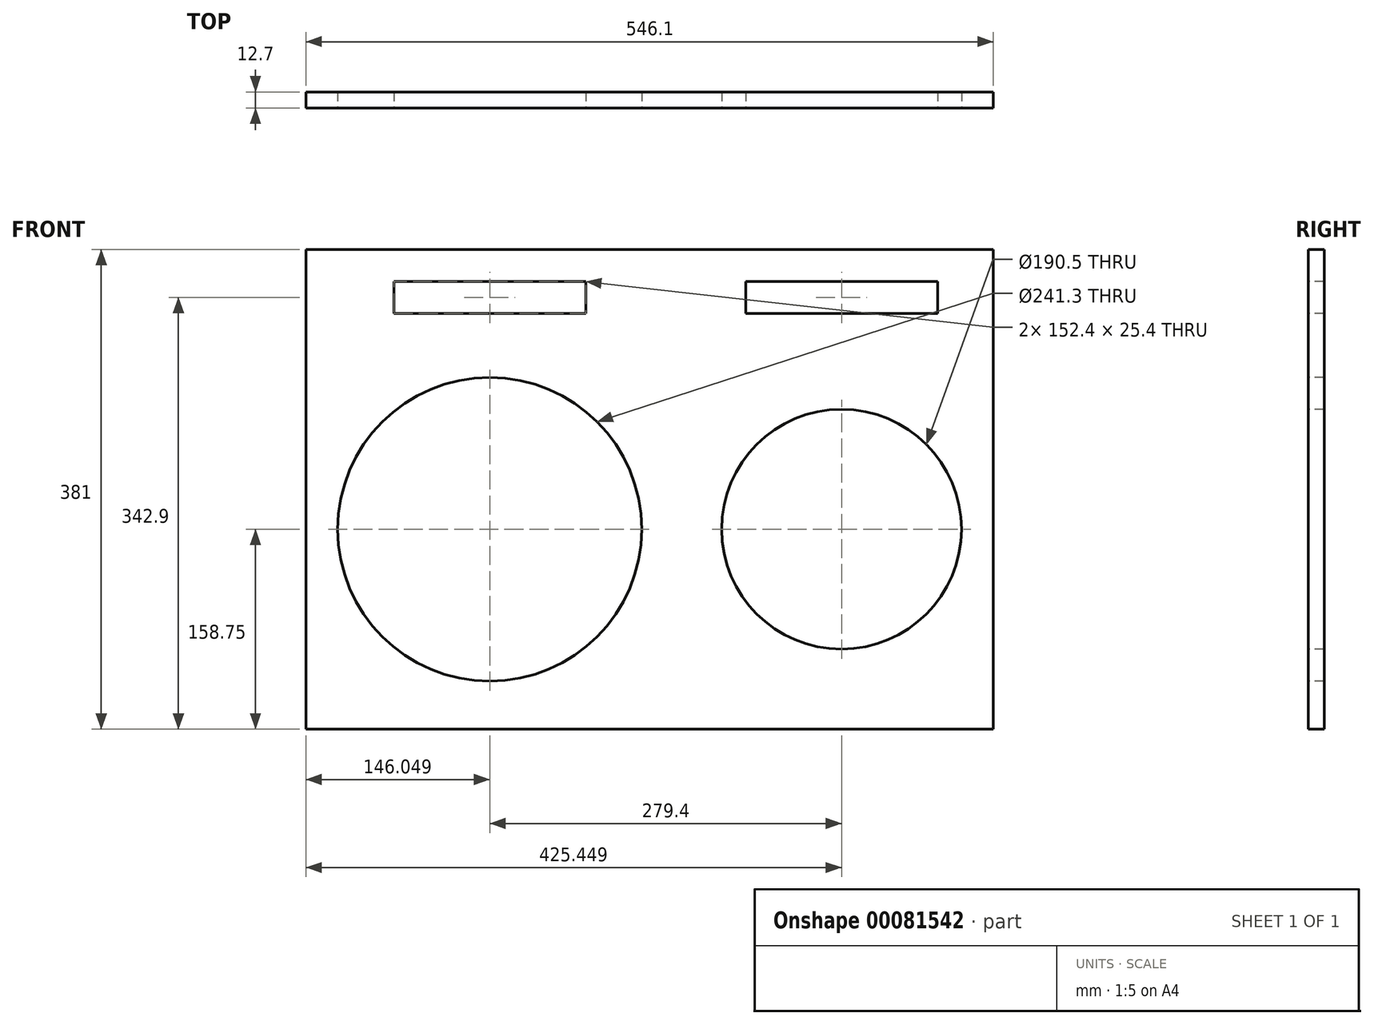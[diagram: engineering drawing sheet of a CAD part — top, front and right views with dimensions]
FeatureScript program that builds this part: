
annotation { "Feature Type Name" : "Feature", "Feature Type Description" : "" }
export const myFeature = defineFeature(function(context is Context, id is Id, definition is map)
    precondition{}
    {
        {
            var Q0;
            Q0=qCreatedBy(makeId("Front.planeOp"),FACE);
            var sketch = newSketch(context, id + "F0", { "sketchPlane" : qUnion([Q0])});
            skLineSegment(sketch, "E0.bottom", {"start": v(280.64, 222.25) * mm, "end": v(-265.46, 222.25) * mm});
            skLineSegment(sketch, "E0.top", {"start": v(280.64, -158.75) * mm, "end": v(-265.46, -158.75) * mm});
            skLineSegment(sketch, "E0.left", {"start": v(280.64, 222.25) * mm, "end": v(280.64, -158.75) * mm});
            skLineSegment(sketch, "E0.right", {"start": v(-265.46, 222.25) * mm, "end": v(-265.46, -158.75) * mm});
            skPoint(sketch, "E0.middle", {"position": v(7.59, 31.75) * mm});
            skCircle(sketch, "E1", {"center": v(-119.41, 0) * mm, "radius": 120.65 * mm});
            skCircle(sketch, "E2", {"center": v(159.99, 0) * mm, "radius": 95.25 * mm});
            skLineSegment(sketch, "E3", {"start": v(-119.41, 0) * mm, "end": v(159.99, 0) * mm, "construction": true});
            skLineSegment(sketch, "E4.bottom", {"start": v(-43.21, 196.85) * mm, "end": v(-195.61, 196.85) * mm});
            skLineSegment(sketch, "E4.top", {"start": v(-43.21, 171.45) * mm, "end": v(-195.61, 171.45) * mm});
            skLineSegment(sketch, "E4.left", {"start": v(-43.21, 196.85) * mm, "end": v(-43.21, 171.45) * mm});
            skLineSegment(sketch, "E4.right", {"start": v(-195.61, 196.85) * mm, "end": v(-195.61, 171.45) * mm});
            skPoint(sketch, "E4.middle", {"position": v(-119.41, 184.15) * mm});
            skLineSegment(sketch, "E5.bottom", {"start": v(83.79, 196.85) * mm, "end": v(236.19, 196.85) * mm});
            skLineSegment(sketch, "E5.top", {"start": v(83.79, 171.45) * mm, "end": v(236.19, 171.45) * mm});
            skLineSegment(sketch, "E5.left", {"start": v(83.79, 196.85) * mm, "end": v(83.79, 171.45) * mm});
            skLineSegment(sketch, "E5.right", {"start": v(236.19, 196.85) * mm, "end": v(236.19, 171.45) * mm});
            skPoint(sketch, "E5.middle", {"position": v(159.99, 184.15) * mm});
            skSolve(sketch);
        }
        {
            var Q0;
            Q0 = qSketchRegion(id + "F0", true);
            extrude(context, id + "F1", {"entities" : qUnion([Q0]), "oppositeDirection" : true, "depth" : 12.7 * mm});
        }
    });
